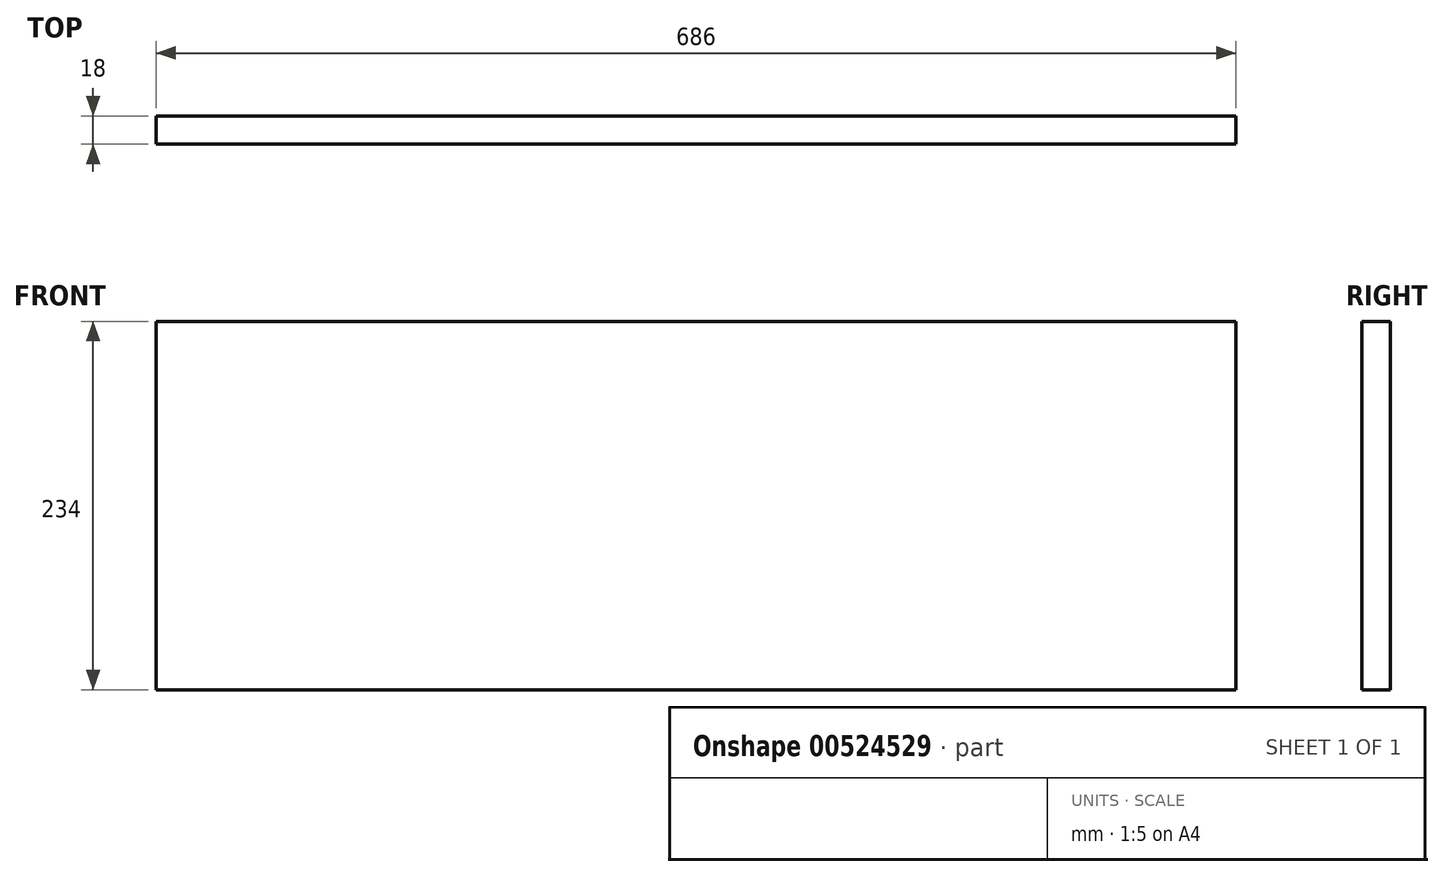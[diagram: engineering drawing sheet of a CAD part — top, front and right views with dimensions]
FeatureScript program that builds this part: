
annotation { "Feature Type Name" : "Feature", "Feature Type Description" : "" }
export const myFeature = defineFeature(function(context is Context, id is Id, definition is map)
    precondition{}
    {
        {
            var Q0;
            Q0=qCreatedBy(makeId("Front.planeOp"),FACE);
            var sketch = newSketch(context, id + "F0", { "sketchPlane" : qUnion([Q0])});
            skLineSegment(sketch, "E0.bottom", {"start": v(0, 0) * mm, "end": v(686, 0) * mm});
            skLineSegment(sketch, "E0.top", {"start": v(0, 234) * mm, "end": v(686, 234) * mm});
            skLineSegment(sketch, "E0.left", {"start": v(0, 0) * mm, "end": v(0, 234) * mm});
            skLineSegment(sketch, "E0.right", {"start": v(686, 0) * mm, "end": v(686, 234) * mm});
            skSolve(sketch);
        }
        {
            var Q0;
            Q0=qSketchRegion(id+"F0",true);
            extrude(context, id + "F1", {"entities" : qUnion([Q0]), "depth" : 18 * mm, "offsetDistance" : 25 * mm});
        }
    });
